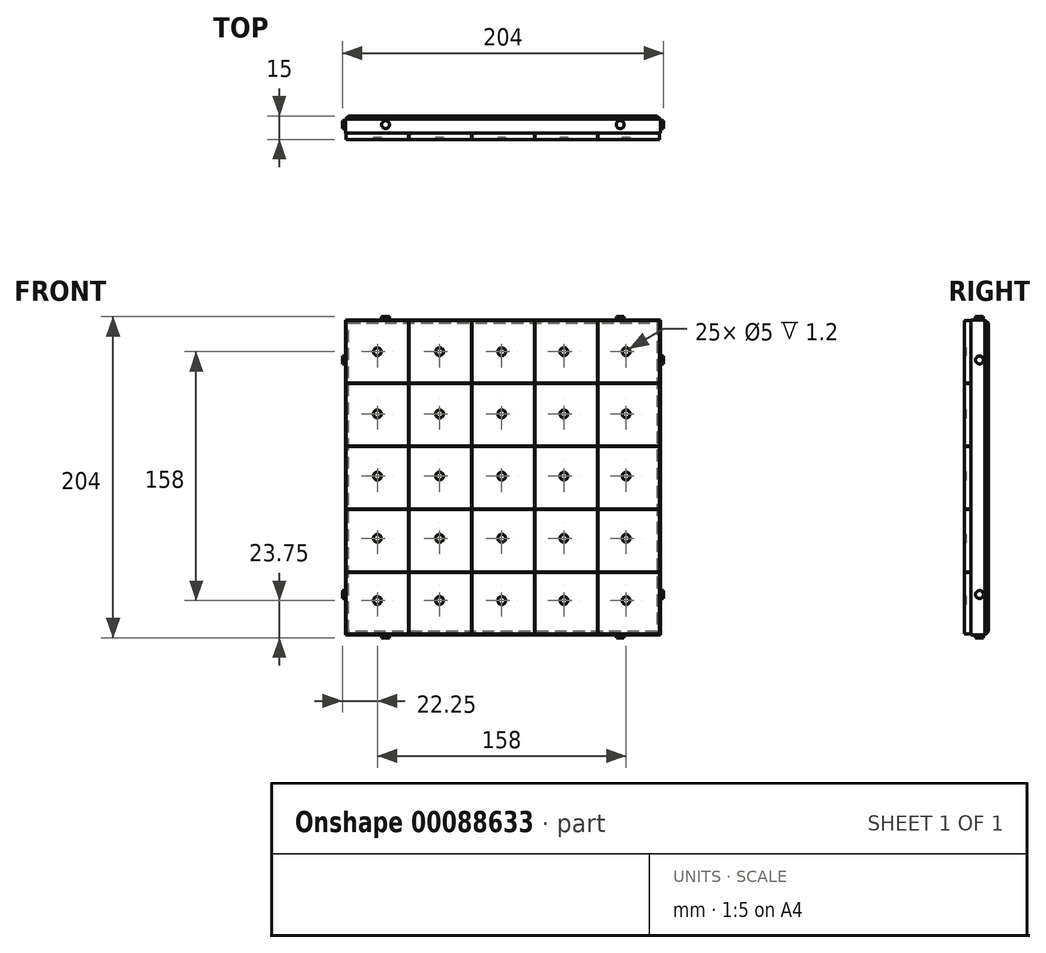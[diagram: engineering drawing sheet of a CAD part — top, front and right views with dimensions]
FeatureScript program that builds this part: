
annotation { "Feature Type Name" : "Feature", "Feature Type Description" : "" }
export const myFeature = defineFeature(function(context is Context, id is Id, definition is map)
    precondition{}
    {
        {
            var Q0;
            Q0=qCreatedBy(makeId("Front.planeOp"),FACE);
            var sketch = newSketch(context, id + "F0", { "sketchPlane" : qUnion([Q0])});
            skLineSegment(sketch, "E0.bottom", {"start": v(100, -100) * mm, "end": v(-100, -100) * mm});
            skLineSegment(sketch, "E0.top", {"start": v(100, 100) * mm, "end": v(-100, 100) * mm});
            skLineSegment(sketch, "E0.left", {"start": v(100, -100) * mm, "end": v(100, 100) * mm});
            skLineSegment(sketch, "E0.right", {"start": v(-100, -100) * mm, "end": v(-100, 100) * mm});
            skPoint(sketch, "E0.middle", {"position": v(0, 0) * mm});
            skSolve(sketch);
        }
        {
            var Q0;
            Q0=makeQuery(id+"F0.imprint","IMPRINT",FACE,{"disambiguationData":[TD([[makeQuery(id+"F0.imprint","IMPRINT",EDGE,{"derivedFrom":sQuery(id+"F0.wireOp",EDGE,"E0.bottom")}),-1.0]])]});
            var Q1;
            Q1=qSketchRegion(id+"F0",true);
            extrude(context, id + "F1", {"entities" : qUnion([Q0, Q1]), "depth" : 15 * mm});
        }
        {
            var Q0;
            Q0=makeQuery(id+"F1.opExtrude","CAP_FACE",FACE,{"disambiguationData":[OSD([sQuery(id+"F0.wireOp",EDGE,"E0.bottom"),sQuery(id+"F0.wireOp",EDGE,"E0.top"),sQuery(id+"F0.wireOp",EDGE,"E0.left"),sQuery(id+"F0.wireOp",EDGE,"E0.right")])],"isStart":false});
            var sketch = newSketch(context, id + "F2", { "sketchPlane" : qUnion([Q0])});
            skLineSegment(sketch, "E1.bottom", {"start": v(-100, 100) * mm, "end": v(100, 100) * mm});
            skLineSegment(sketch, "E1.top", {"start": v(-100, 99.5) * mm, "end": v(100, 99.5) * mm});
            skLineSegment(sketch, "E1.left", {"start": v(-100, 100) * mm, "end": v(-100, 99.5) * mm});
            skLineSegment(sketch, "E1.right", {"start": v(100, 100) * mm, "end": v(100, 99.5) * mm});
            skLineSegment(sketch, "E2.0.1.0", {"start": v(-100, 59.5) * mm, "end": v(100, 59.5) * mm});
            skLineSegment(sketch, "E2.0.1.1", {"start": v(-100, 60) * mm, "end": v(100, 60) * mm});
            skLineSegment(sketch, "E2.0.1.2", {"start": v(100, 60) * mm, "end": v(100, 59.5) * mm});
            skLineSegment(sketch, "E2.0.1.3", {"start": v(-100, 60) * mm, "end": v(-100, 59.5) * mm});
            skLineSegment(sketch, "E2.0.2.0", {"start": v(-100, 19.5) * mm, "end": v(100, 19.5) * mm});
            skLineSegment(sketch, "E2.0.2.1", {"start": v(-100, 20) * mm, "end": v(100, 20) * mm});
            skLineSegment(sketch, "E2.0.2.2", {"start": v(100, 20) * mm, "end": v(100, 19.5) * mm});
            skLineSegment(sketch, "E2.0.2.3", {"start": v(-100, 20) * mm, "end": v(-100, 19.5) * mm});
            skLineSegment(sketch, "E2.0.3.0", {"start": v(-100, -20.5) * mm, "end": v(100, -20.5) * mm});
            skLineSegment(sketch, "E2.0.3.1", {"start": v(-100, -20) * mm, "end": v(100, -20) * mm});
            skLineSegment(sketch, "E2.0.3.2", {"start": v(100, -20) * mm, "end": v(100, -20.5) * mm});
            skLineSegment(sketch, "E2.0.3.3", {"start": v(-100, -20) * mm, "end": v(-100, -20.5) * mm});
            skLineSegment(sketch, "E2.0.4.0", {"start": v(-100, -60.5) * mm, "end": v(100, -60.5) * mm});
            skLineSegment(sketch, "E2.0.4.1", {"start": v(-100, -60) * mm, "end": v(100, -60) * mm});
            skLineSegment(sketch, "E2.0.4.2", {"start": v(100, -60) * mm, "end": v(100, -60.5) * mm});
            skLineSegment(sketch, "E2.0.4.3", {"start": v(-100, -60) * mm, "end": v(-100, -60.5) * mm});
            skLineSegment(sketch, "E2.direction1", {"start": v(-100, 99.5) * mm, "end": v(-99.9, 99.5) * mm, "construction": true});
            skLineSegment(sketch, "E2.direction2", {"start": v(-100, 99.5) * mm, "end": v(-100, 59.5) * mm, "construction": true});
            skLineSegment(sketch, "E3.0.0.5", {"start": v(-100, -100.5) * mm, "end": v(100, -100.5) * mm});
            skLineSegment(sketch, "E3.3.0.5", {"start": v(-100, -100) * mm, "end": v(100, -100) * mm});
            skLineSegment(sketch, "E3.6.0.5", {"start": v(100, -100) * mm, "end": v(100, -100.5) * mm});
            skLineSegment(sketch, "E3.9.0.5", {"start": v(-100, -100) * mm, "end": v(-100, -100.5) * mm});
            skSolve(sketch);
        }
        {
            var Q0;
            Q0=qSketchRegion(id+"F0",true);
            extrude(context, id + "F3", {"entities" : qUnion([Q0]), "depth" : 5 * mm});
        }
        {
            var Q0;
            Q0=qSketchRegion(id+"F2",true);
            extrude(context, id + "F4", {"entities" : qUnion([Q0]), "operationType" : NewBodyOperationType.REMOVE, "oppositeDirection" : true, "depth" : 4 * mm});
        }
        {
            var Q0;
            {var subQ0=sQuery(id+"F0.wireOp",EDGE,"E0.left");var subQ1=sQuery(id+"F0.wireOp",EDGE,"E0.right");Q0=makeQuery(id+"F4.boolean.opBoolean","SPLIT",FACE,{"disambiguationData":[TD([makeQuery(id+"F4.opExtrude","SWEPT_FACE",FACE,{"disambiguationData":[OSD([sQuery(id+"F2.wireOp",EDGE,"E1.top"),sQuery(id+"F2.wireOp",EDGE,"E2.1.0.0"),sQuery(id+"F2.wireOp",EDGE,"E2.2.0.0")])]})])],"derivedFrom":makeQuery(id+"F1.opExtrude","CAP_FACE",FACE,{"disambiguationData":[OSD([sQuery(id+"F0.wireOp",EDGE,"E0.bottom"),sQuery(id+"F0.wireOp",EDGE,"E0.top"),subQ0,subQ1])],"isStart":false})});}
            var sketch = newSketch(context, id + "F5", { "sketchPlane" : qUnion([Q0])});
            skLineSegment(sketch, "E4.bottom", {"start": v(-100, 100) * mm, "end": v(-99.5, 100) * mm});
            skLineSegment(sketch, "E4.top", {"start": v(-100, -100) * mm, "end": v(-99.5, -100) * mm});
            skLineSegment(sketch, "E4.left", {"start": v(-100, 100) * mm, "end": v(-100, -100) * mm});
            skLineSegment(sketch, "E4.right", {"start": v(-99.5, 100) * mm, "end": v(-99.5, -100) * mm});
            skLineSegment(sketch, "E5.1.0.0", {"start": v(-59.5, 100) * mm, "end": v(-59.5, -100) * mm});
            skLineSegment(sketch, "E5.1.0.1", {"start": v(-60, 100) * mm, "end": v(-60, -100) * mm});
            skLineSegment(sketch, "E5.1.0.2", {"start": v(-60, -100) * mm, "end": v(-59.5, -100) * mm});
            skLineSegment(sketch, "E5.1.0.3", {"start": v(-60, 100) * mm, "end": v(-59.5, 100) * mm});
            skLineSegment(sketch, "E5.2.0.0", {"start": v(-19.5, 100) * mm, "end": v(-19.5, -100) * mm});
            skLineSegment(sketch, "E5.2.0.1", {"start": v(-20, 100) * mm, "end": v(-20, -100) * mm});
            skLineSegment(sketch, "E5.2.0.2", {"start": v(-20, -100) * mm, "end": v(-19.5, -100) * mm});
            skLineSegment(sketch, "E5.2.0.3", {"start": v(-20, 100) * mm, "end": v(-19.5, 100) * mm});
            skLineSegment(sketch, "E5.3.0.0", {"start": v(20.5, 100) * mm, "end": v(20.5, -100) * mm});
            skLineSegment(sketch, "E5.3.0.1", {"start": v(20, 100) * mm, "end": v(20, -100) * mm});
            skLineSegment(sketch, "E5.3.0.2", {"start": v(20, -100) * mm, "end": v(20.5, -100) * mm});
            skLineSegment(sketch, "E5.3.0.3", {"start": v(20, 100) * mm, "end": v(20.5, 100) * mm});
            skLineSegment(sketch, "E5.4.0.0", {"start": v(60.5, 100) * mm, "end": v(60.5, -100) * mm});
            skLineSegment(sketch, "E5.4.0.1", {"start": v(60, 100) * mm, "end": v(60, -100) * mm});
            skLineSegment(sketch, "E5.4.0.2", {"start": v(60, -100) * mm, "end": v(60.5, -100) * mm});
            skLineSegment(sketch, "E5.4.0.3", {"start": v(60, 100) * mm, "end": v(60.5, 100) * mm});
            skLineSegment(sketch, "E5.direction1", {"start": v(-99.5, -100) * mm, "end": v(-59.5, -100) * mm, "construction": true});
            skLineSegment(sketch, "E6.0.5.0", {"start": v(100.5, 100) * mm, "end": v(100.5, -100) * mm});
            skLineSegment(sketch, "E6.3.5.0", {"start": v(100, 100) * mm, "end": v(100, -100) * mm});
            skLineSegment(sketch, "E6.6.5.0", {"start": v(100, -100) * mm, "end": v(100.5, -100) * mm});
            skLineSegment(sketch, "E6.9.5.0", {"start": v(100, 100) * mm, "end": v(100.5, 100) * mm});
            skSolve(sketch);
        }
        {
            var Q0;
            Q0=qSketchRegion(id+"F5",true);
            extrude(context, id + "F6", {"entities" : qUnion([Q0]), "operationType" : NewBodyOperationType.REMOVE, "oppositeDirection" : true, "depth" : 4 * mm});
        }
        {
            var Q0;
            {var subQ0=sQuery(id+"F0.wireOp",EDGE,"E0.bottom");var subQ1=makeQuery(id+"F1.opExtrude","SWEPT_FACE",FACE,{"disambiguationData":[OSD([subQ0])]});var subQ2=sQuery(id+"F0.wireOp",EDGE,"E0.left");var subQ3=makeQuery(id+"F1.opExtrude","SWEPT_FACE",FACE,{"disambiguationData":[OSD([subQ2])]});var subQ5=sQuery(id+"F0.wireOp",EDGE,"E0.right");Q0=makeQuery(id+"F6.boolean.opBoolean","SPLIT",FACE,{"disambiguationData":[TD([subQ3])],"derivedFrom":makeQuery(id+"F4.boolean.opBoolean","SPLIT",FACE,{"disambiguationData":[TD([subQ1])],"derivedFrom":makeQuery(id+"F1.opExtrude","CAP_FACE",FACE,{"disambiguationData":[OSD([subQ0,sQuery(id+"F0.wireOp",EDGE,"E0.top"),subQ2,subQ5])],"isStart":false})})});}
            var sketch = newSketch(context, id + "F7", { "sketchPlane" : qUnion([Q0])});
            skLineSegment(sketch, "E7.bottom", {"start": v(-100, -100) * mm, "end": v(100, -100) * mm});
            skLineSegment(sketch, "E7.top", {"start": v(-100, -99.5) * mm, "end": v(99.5, -99.5) * mm});
            skLineSegment(sketch, "E7.left", {"start": v(-100, -100) * mm, "end": v(-100, -99.5) * mm});
            skLineSegment(sketch, "E7.right", {"start": v(100, -100) * mm, "end": v(100, -99.5) * mm});
            skLineSegment(sketch, "E8.bottom", {"start": v(100, -100) * mm, "end": v(99.5, -100) * mm});
            skLineSegment(sketch, "E8.top", {"start": v(100, 99.5) * mm, "end": v(99.5, 99.5) * mm});
            skLineSegment(sketch, "E8.left", {"start": v(100, -100) * mm, "end": v(100, 99.5) * mm});
            skLineSegment(sketch, "E8.right", {"start": v(99.5, -99.5) * mm, "end": v(99.5, 99.5) * mm});
            skSolve(sketch);
        }
        {
            var Q0;
            Q0=qSketchRegion(id+"F7",true);
            extrude(context, id + "F8", {"entities" : qUnion([Q0]), "operationType" : NewBodyOperationType.REMOVE, "oppositeDirection" : true, "depth" : 4 * mm});
        }
        {
            var Q0;
            {var subQ0=makeQuery(id+"F4.opExtrude","SWEPT_FACE",FACE,{"disambiguationData":[OSD([sQuery(id+"F2.wireOp",EDGE,"E1.top")])]});var subQ2=sQuery(id+"F0.wireOp",EDGE,"E0.left");var subQ3=sQuery(id+"F0.wireOp",EDGE,"E0.right");Q0=makeQuery(id+"F6.boolean.opBoolean","SPLIT",FACE,{"disambiguationData":[TD([makeQuery(id+"F6.opExtrude","SWEPT_FACE",FACE,{"disambiguationData":[OSD([sQuery(id+"F5.wireOp",EDGE,"E4.right")])]})])],"derivedFrom":makeQuery(id+"F4.boolean.opBoolean","SPLIT",FACE,{"disambiguationData":[TD([subQ0])],"derivedFrom":makeQuery(id+"F1.opExtrude","CAP_FACE",FACE,{"disambiguationData":[OSD([sQuery(id+"F0.wireOp",EDGE,"E0.bottom"),sQuery(id+"F0.wireOp",EDGE,"E0.top"),subQ2,subQ3])],"isStart":false})})});}
            var sketch = newSketch(context, id + "F9", { "sketchPlane" : qUnion([Q0])});
            skPoint(sketch, "E9", {"position": v(-79.75, 79.75) * mm});
            skPoint(sketch, "E9.positionSnap0", {"position": v(-99.5, 79.75) * mm});
            skPoint(sketch, "E9.positionSnap1", {"position": v(-79.75, 99.5) * mm});
            skCircle(sketch, "E10", {"center": v(-79.75, 79.75) * mm, "radius": 2.5 * mm});
            skCircle(sketch, "E11.0.1.0", {"center": v(-79.75, 40.25) * mm, "radius": 2.5 * mm});
            skCircle(sketch, "E11.0.2.0", {"center": v(-79.75, 0.75) * mm, "radius": 2.5 * mm});
            skCircle(sketch, "E11.0.3.0", {"center": v(-79.75, -38.75) * mm, "radius": 2.5 * mm});
            skCircle(sketch, "E11.0.4.0", {"center": v(-79.75, -78.25) * mm, "radius": 2.5 * mm});
            skCircle(sketch, "E11.1.0.0", {"center": v(-40.25, 79.75) * mm, "radius": 2.5 * mm});
            skCircle(sketch, "E11.1.1.0", {"center": v(-40.25, 40.25) * mm, "radius": 2.5 * mm});
            skCircle(sketch, "E11.1.2.0", {"center": v(-40.25, 0.75) * mm, "radius": 2.5 * mm});
            skCircle(sketch, "E11.1.3.0", {"center": v(-40.25, -38.75) * mm, "radius": 2.5 * mm});
            skCircle(sketch, "E11.1.4.0", {"center": v(-40.25, -78.25) * mm, "radius": 2.5 * mm});
            skCircle(sketch, "E11.2.0.0", {"center": v(-0.75, 79.75) * mm, "radius": 2.5 * mm});
            skCircle(sketch, "E11.2.1.0", {"center": v(-0.75, 40.25) * mm, "radius": 2.5 * mm});
            skCircle(sketch, "E11.2.2.0", {"center": v(-0.75, 0.75) * mm, "radius": 2.5 * mm});
            skCircle(sketch, "E11.2.3.0", {"center": v(-0.75, -38.75) * mm, "radius": 2.5 * mm});
            skCircle(sketch, "E11.2.4.0", {"center": v(-0.75, -78.25) * mm, "radius": 2.5 * mm});
            skCircle(sketch, "E11.3.0.0", {"center": v(38.75, 79.75) * mm, "radius": 2.5 * mm});
            skCircle(sketch, "E11.3.1.0", {"center": v(38.75, 40.25) * mm, "radius": 2.5 * mm});
            skCircle(sketch, "E11.3.2.0", {"center": v(38.75, 0.75) * mm, "radius": 2.5 * mm});
            skCircle(sketch, "E11.3.3.0", {"center": v(38.75, -38.75) * mm, "radius": 2.5 * mm});
            skCircle(sketch, "E11.3.4.0", {"center": v(38.75, -78.25) * mm, "radius": 2.5 * mm});
            skCircle(sketch, "E11.4.0.0", {"center": v(78.25, 79.75) * mm, "radius": 2.5 * mm});
            skCircle(sketch, "E11.4.1.0", {"center": v(78.25, 40.25) * mm, "radius": 2.5 * mm});
            skCircle(sketch, "E11.4.2.0", {"center": v(78.25, 0.75) * mm, "radius": 2.5 * mm});
            skCircle(sketch, "E11.4.3.0", {"center": v(78.25, -38.75) * mm, "radius": 2.5 * mm});
            skCircle(sketch, "E11.4.4.0", {"center": v(78.25, -78.25) * mm, "radius": 2.5 * mm});
            skLineSegment(sketch, "E11.direction1", {"start": v(-79.75, 79.75) * mm, "end": v(-40.25, 79.75) * mm, "construction": true});
            skLineSegment(sketch, "E11.direction2", {"start": v(-79.75, 79.75) * mm, "end": v(-79.75, 40.25) * mm, "construction": true});
            skSolve(sketch);
        }
        {
            var Q0;
            Q0=qSketchRegion(id+"F9",true);
            extrude(context, id + "F10", {"entities" : qUnion([Q0]), "operationType" : NewBodyOperationType.REMOVE, "oppositeDirection" : true, "depth" : 1.2 * mm});
        }
        {
            var Q0;
            Q0=makeQuery(id+"F1.opExtrude","SWEPT_FACE",FACE,{"disambiguationData":[OSD([sQuery(id+"F0.wireOp",EDGE,"E0.left")])]});
            var sketch = newSketch(context, id + "F11", { "sketchPlane" : qUnion([Q0])});
            skCircle(sketch, "E12", {"center": v(-5.5, -74.5) * mm, "radius": 2.5 * mm});
            skCircle(sketch, "E13", {"center": v(-5.5, 74.5) * mm, "radius": 2.5 * mm});
            skSolve(sketch);
        }
        {
            var Q0;
            Q0=qSketchRegion(id+"F11",true);
            extrude(context, id + "F12", {"entities" : qUnion([Q0]), "operationType" : NewBodyOperationType.ADD, "depth" : 2 * mm});
        }
        {
            var Q0;
            Q0=makeQuery(id+"F1.opExtrude","SWEPT_FACE",FACE,{"disambiguationData":[OSD([sQuery(id+"F0.wireOp",EDGE,"E0.bottom")])]});
            var sketch = newSketch(context, id + "F13", { "sketchPlane" : qUnion([Q0])});
            skCircle(sketch, "E14", {"center": v(-74.5, 5.5) * mm, "radius": 2.5 * mm});
            skCircle(sketch, "E15", {"center": v(74.5, 5.5) * mm, "radius": 2.5 * mm});
            skSolve(sketch);
        }
        {
            var Q0;
            Q0=qSketchRegion(id+"F13",true);
            extrude(context, id + "F14", {"entities" : qUnion([Q0]), "operationType" : NewBodyOperationType.ADD, "depth" : 2 * mm});
        }
        {
            var Q0;
            Q0=makeQuery(id+"F1.opExtrude","CAP_FACE",FACE,{"disambiguationData":[OSD([sQuery(id+"F0.wireOp",EDGE,"E0.bottom"),sQuery(id+"F0.wireOp",EDGE,"E0.top"),sQuery(id+"F0.wireOp",EDGE,"E0.left"),sQuery(id+"F0.wireOp",EDGE,"E0.right")])],"isStart":true});
            chamfer(context, id + "F15", {"entities" : qUnion([Q0]), "width" : 2 * mm, "tangentPropagation" : true});
        }
        {
            var Q0;
            Q0=makeQuery(id+"F1.opExtrude","SWEPT_FACE",FACE,{"disambiguationData":[OSD([sQuery(id+"F0.wireOp",EDGE,"E0.right")])]});
            var sketch = newSketch(context, id + "F16", { "sketchPlane" : qUnion([Q0])});
            skCircle(sketch, "E16", {"center": v(5.5, -74.5) * mm, "radius": 2.5 * mm});
            skCircle(sketch, "E17", {"center": v(5.5, 74.5) * mm, "radius": 2.5 * mm});
            skSolve(sketch);
        }
        {
            var Q0;
            Q0=qSketchRegion(id+"F16",true);
            extrude(context, id + "F17", {"entities" : qUnion([Q0]), "operationType" : NewBodyOperationType.ADD, "depth" : 2 * mm});
        }
        {
            var Q0;
            Q0=makeQuery(id+"F1.opExtrude","SWEPT_FACE",FACE,{"disambiguationData":[OSD([sQuery(id+"F0.wireOp",EDGE,"E0.top")])]});
            var sketch = newSketch(context, id + "F18", { "sketchPlane" : qUnion([Q0])});
            skCircle(sketch, "E18", {"center": v(74.5, -5.5) * mm, "radius": 2.5 * mm});
            skCircle(sketch, "E19", {"center": v(-74.5, -5.5) * mm, "radius": 2.5 * mm});
            skSolve(sketch);
        }
        {
            var Q0;
            Q0=qSketchRegion(id+"F18",true);
            extrude(context, id + "F19", {"entities" : qUnion([Q0]), "operationType" : NewBodyOperationType.ADD, "depth" : 2 * mm});
        }
    });
